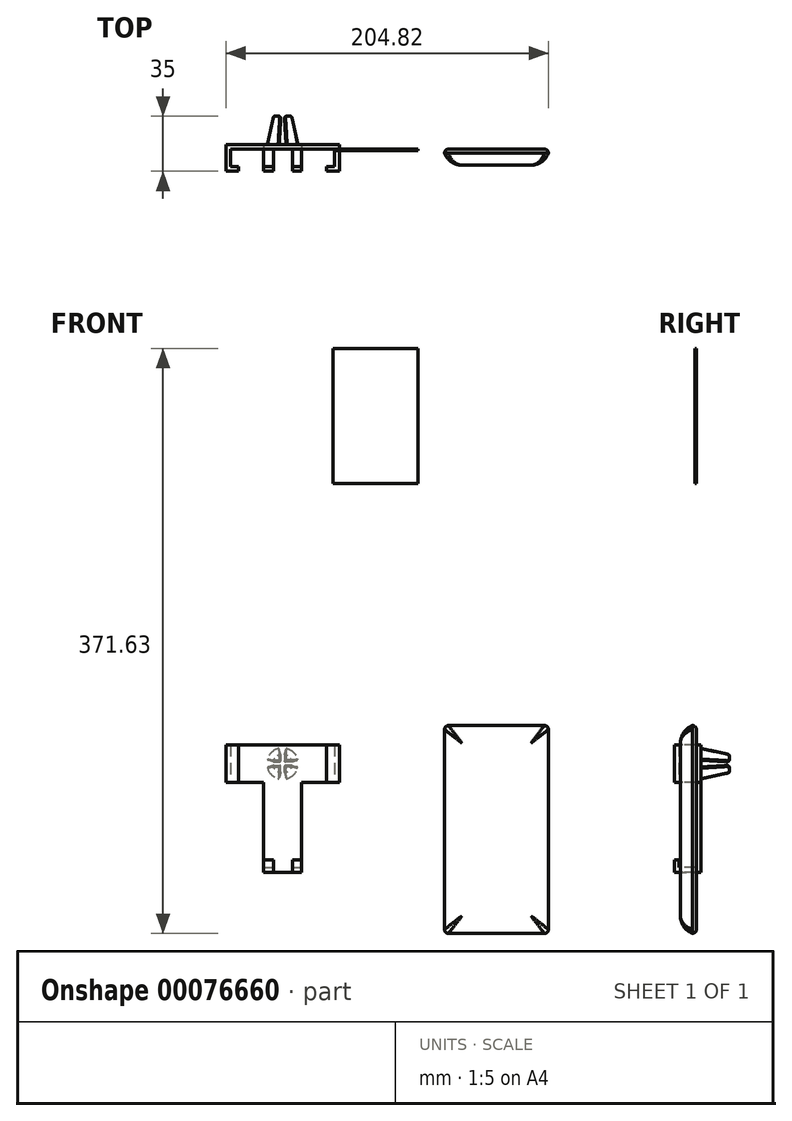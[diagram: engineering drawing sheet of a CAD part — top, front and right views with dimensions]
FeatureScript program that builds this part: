
annotation { "Feature Type Name" : "Feature", "Feature Type Description" : "" }
export const myFeature = defineFeature(function(context is Context, id is Id, definition is map)
    precondition{}
    {
        {
            var Q0;
            Q0=qCreatedBy(makeId("Front.planeOp"),FACE);
            var sketch = newSketch(context, id + "F0", { "sketchPlane" : qUnion([Q0])});
            skCircle(sketch, "E0", {"center": v(0, 0) * mm, "radius": 10 * mm});
            skSolve(sketch);
        }
        {
            var Q0;
            Q0 = qSketchRegion(id + "F0", true);
            extrude(context, id + "F1", {"entities" : qUnion([Q0]), "oppositeDirection" : true, "depth" : 3 * mm});
        }
        {
            var Q0;
            Q0=makeQuery(id+"F1.opExtrude","CAP_FACE",FACE,{"disambiguationData":[OSD([sQuery(id+"F0.wireOp",EDGE,"E0")])],"isStart":false});
            var sketch = newSketch(context, id + "F2", { "sketchPlane" : qUnion([Q0])});
            skLineSegment(sketch, "E1.top", {"start": v(-9.75, 2.2) * mm, "end": v(-2.2, 2.2) * mm});
            skLineSegment(sketch, "E1.right", {"start": v(-2.2, 9.75) * mm, "end": v(-2.2, 2.2) * mm});
            skArc(sketch, "E2", {"start": v(-2.2, 9.75) * mm, "mid": v(-7.07, 7.07) * mm, "end": v(-9.75, 2.2) * mm});
            skLineSegment(sketch, "E3.1.0", {"start": v(-9.75, -2.2) * mm, "end": v(-2.2, -2.2) * mm});
            skLineSegment(sketch, "E3.1.1", {"start": v(-2.2, -9.75) * mm, "end": v(-2.2, -2.2) * mm});
            skArc(sketch, "E3.1.2", {"start": v(-9.75, -2.2) * mm, "mid": v(-7.07, -7.07) * mm, "end": v(-2.2, -9.75) * mm});
            skLineSegment(sketch, "E3.2.0", {"start": v(2.2, -9.75) * mm, "end": v(2.2, -2.2) * mm});
            skLineSegment(sketch, "E3.2.1", {"start": v(9.75, -2.2) * mm, "end": v(2.2, -2.2) * mm});
            skArc(sketch, "E3.2.2", {"start": v(2.2, -9.75) * mm, "mid": v(7.07, -7.07) * mm, "end": v(9.75, -2.2) * mm});
            skLineSegment(sketch, "E4.2.3.0", {"start": v(9.75, 2.2) * mm, "end": v(2.2, 2.2) * mm});
            skLineSegment(sketch, "E4.3.3.0", {"start": v(2.2, 9.75) * mm, "end": v(2.2, 2.2) * mm});
            skArc(sketch, "E4.6.3.0", {"start": v(9.75, 2.2) * mm, "mid": v(7.07, 7.07) * mm, "end": v(2.2, 9.75) * mm});
            skSolve(sketch);
        }
        {
            var Q0;
            Q0=makeQuery(id+"F2.imprint","IMPRINT",FACE,{"disambiguationData":[TD([[makeQuery(id+"F2.imprint","IMPRINT",EDGE,{"derivedFrom":sQuery(id+"F2.wireOp",EDGE,"E1.top")}),-1.0]])]});
            cPlane(context, id + "F3", {"entities" : qUnion([Q0]), "cplaneType" : CPlaneType.OFFSET, "offset" : 18 * mm, "width" : 150 * mm, "height" : 150 * mm});
        }
        {
            var Q0;
            Q0=qCreatedBy(id+"F3.planeOp",FACE);
            var sketch = newSketch(context, id + "F4", { "sketchPlane" : qUnion([Q0])});
            skLineSegment(sketch, "E5.top", {"start": v(-5.9, 1.1) * mm, "end": v(-1.1, 1.1) * mm});
            skLineSegment(sketch, "E5.right", {"start": v(-1.1, 5.9) * mm, "end": v(-1.1, 1.1) * mm});
            skArc(sketch, "E6", {"start": v(-1.1, 5.9) * mm, "mid": v(-4.24, 4.24) * mm, "end": v(-5.9, 1.1) * mm});
            skLineSegment(sketch, "E7.1.0", {"start": v(-5.9, -1.1) * mm, "end": v(-1.1, -1.1) * mm});
            skLineSegment(sketch, "E7.1.1", {"start": v(-1.1, -5.9) * mm, "end": v(-1.1, -1.1) * mm});
            skArc(sketch, "E7.1.2", {"start": v(-5.9, -1.1) * mm, "mid": v(-4.24, -4.24) * mm, "end": v(-1.1, -5.9) * mm});
            skLineSegment(sketch, "E7.2.0", {"start": v(1.1, -5.9) * mm, "end": v(1.1, -1.1) * mm});
            skLineSegment(sketch, "E7.2.1", {"start": v(5.9, -1.1) * mm, "end": v(1.1, -1.1) * mm});
            skArc(sketch, "E7.2.2", {"start": v(1.1, -5.9) * mm, "mid": v(4.24, -4.24) * mm, "end": v(5.9, -1.1) * mm});
            skLineSegment(sketch, "E7.3.0", {"start": v(5.9, 1.1) * mm, "end": v(1.1, 1.1) * mm});
            skLineSegment(sketch, "E7.3.1", {"start": v(1.1, 5.9) * mm, "end": v(1.1, 1.1) * mm});
            skArc(sketch, "E7.3.2", {"start": v(5.9, 1.1) * mm, "mid": v(4.24, 4.24) * mm, "end": v(1.1, 5.9) * mm});
            skSolve(sketch);
        }
        {
            var Q1;
            Q1=makeQuery(id+"F4.imprint","IMPRINT",FACE,{"disambiguationData":[TD([[makeQuery(id+"F4.imprint","IMPRINT",EDGE,{"derivedFrom":sQuery(id+"F4.wireOp",EDGE,"E5.top")}),1.0]])]});
            var Q2;
            Q2=makeQuery(id+"F2.imprint","IMPRINT",FACE,{"disambiguationData":[TD([[makeQuery(id+"F2.imprint","IMPRINT",EDGE,{"derivedFrom":sQuery(id+"F2.wireOp",EDGE,"E1.top")}),1.0]])]});
            loft(context, id + "F5", {"operationType" : NewBodyOperationType.ADD, "sheetProfilesArray" : [{ "sheetProfileEntities" : qUnion([Q1]) }, { "sheetProfileEntities" : qUnion([Q2]) }]});
        }
        {
            var Q1;
            Q1=makeQuery(id+"F2.imprint","IMPRINT",FACE,{"disambiguationData":[TD([[makeQuery(id+"F2.imprint","IMPRINT",EDGE,{"derivedFrom":sQuery(id+"F2.wireOp",EDGE,"E4.2.3.0")}),-1.0]])]});
            var Q2;
            Q2=makeQuery(id+"F4.imprint","IMPRINT",FACE,{"disambiguationData":[TD([[makeQuery(id+"F4.imprint","IMPRINT",EDGE,{"derivedFrom":sQuery(id+"F4.wireOp",EDGE,"E7.3.0")}),-1.0]])]});
            loft(context, id + "F6", {"operationType" : NewBodyOperationType.ADD, "sheetProfilesArray" : [{ "sheetProfileEntities" : qUnion([Q1]) }, { "sheetProfileEntities" : qUnion([Q2]) }]});
        }
        {
            var Q1;
            Q1=makeQuery(id+"F2.imprint","IMPRINT",FACE,{"disambiguationData":[TD([[makeQuery(id+"F2.imprint","IMPRINT",EDGE,{"derivedFrom":sQuery(id+"F2.wireOp",EDGE,"E3.1.0")}),-1.0]])]});
            var Q2;
            Q2=makeQuery(id+"F4.imprint","IMPRINT",FACE,{"disambiguationData":[TD([[makeQuery(id+"F4.imprint","IMPRINT",EDGE,{"derivedFrom":sQuery(id+"F4.wireOp",EDGE,"E7.1.0")}),-1.0]])]});
            loft(context, id + "F7", {"operationType" : NewBodyOperationType.ADD, "sheetProfilesArray" : [{ "sheetProfileEntities" : qUnion([Q1]) }, { "sheetProfileEntities" : qUnion([Q2]) }]});
        }
        {
            var Q1;
            Q1=makeQuery(id+"F2.imprint","IMPRINT",FACE,{"disambiguationData":[TD([[makeQuery(id+"F2.imprint","IMPRINT",EDGE,{"derivedFrom":sQuery(id+"F2.wireOp",EDGE,"E3.2.0")}),-1.0]])]});
            var Q2;
            Q2=makeQuery(id+"F4.imprint","IMPRINT",FACE,{"disambiguationData":[TD([[makeQuery(id+"F4.imprint","IMPRINT",EDGE,{"derivedFrom":sQuery(id+"F4.wireOp",EDGE,"E7.2.0")}),-1.0]])]});
            loft(context, id + "F8", {"operationType" : NewBodyOperationType.ADD, "sheetProfilesArray" : [{ "sheetProfileEntities" : qUnion([Q1]) }, { "sheetProfileEntities" : qUnion([Q2]) }]});
        }
        {
            var Q0;
            {var subQ0=sQuery(id+"F4.wireOp",EDGE,"E6");var subQ1=sQuery(id+"F4.wireOp",EDGE,"E5.right");var subQ2=sQuery(id+"F4.wireOp",EDGE,"E5.top");Q0=makeQuery(id+"F5.opLoft","MID_CAP_EDGE",EDGE,{"disambiguationData":[OSD([subQ2,subQ1,subQ0]),TDD([makeQuery(id+"F4.imprint","INTERSECT",VERTEX,{"derivedFrom":[subQ2,subQ0]}),makeQuery(id+"F4.imprint","INTERSECT",VERTEX,{"derivedFrom":[subQ1,subQ0]}),makeQuery(id+"F4.imprint","IMPRINT",EDGE,{"derivedFrom":subQ0})])],"capPos":0.0});}
            var Q1;
            Q1=makeQuery(id+"F5.opLoft","SWEPT_EDGE",EDGE,{"disambiguationData":[OSD([sQuery(id+"F2.wireOp",EDGE,"E1.right"),sQuery(id+"F2.wireOp",EDGE,"E2"),sQuery(id+"F4.wireOp",EDGE,"E5.right"),sQuery(id+"F4.wireOp",EDGE,"E6")])]});
            var Q2;
            Q2=makeQuery(id+"F5.opLoft","SWEPT_EDGE",EDGE,{"disambiguationData":[OSD([sQuery(id+"F2.wireOp",EDGE,"E1.top"),sQuery(id+"F2.wireOp",EDGE,"E1.right"),sQuery(id+"F4.wireOp",EDGE,"E5.top"),sQuery(id+"F4.wireOp",EDGE,"E5.right")])]});
            var Q3;
            Q3=makeQuery(id+"F5.opLoft","SWEPT_EDGE",EDGE,{"disambiguationData":[OSD([sQuery(id+"F2.wireOp",EDGE,"E1.top"),sQuery(id+"F2.wireOp",EDGE,"E2"),sQuery(id+"F4.wireOp",EDGE,"E5.top"),sQuery(id+"F4.wireOp",EDGE,"E6")])]});
            var Q4;
            {var subQ0=sQuery(id+"F4.wireOp",EDGE,"E7.1.2");var subQ1=sQuery(id+"F4.wireOp",EDGE,"E7.1.1");var subQ2=sQuery(id+"F4.wireOp",EDGE,"E7.1.0");Q4=makeQuery(id+"F7.opLoft","MID_CAP_EDGE",EDGE,{"disambiguationData":[OSD([subQ2,subQ1,subQ0]),TDD([makeQuery(id+"F4.imprint","INTERSECT",VERTEX,{"derivedFrom":[subQ2,subQ0]}),makeQuery(id+"F4.imprint","INTERSECT",VERTEX,{"derivedFrom":[subQ1,subQ0]}),makeQuery(id+"F4.imprint","IMPRINT",EDGE,{"derivedFrom":subQ0})])],"capPos":1.0});}
            var Q5;
            Q5=makeQuery(id+"F7.opLoft","SWEPT_EDGE",EDGE,{"disambiguationData":[OSD([sQuery(id+"F2.wireOp",EDGE,"E3.1.0"),sQuery(id+"F2.wireOp",EDGE,"E3.1.2"),sQuery(id+"F4.wireOp",EDGE,"E7.1.0"),sQuery(id+"F4.wireOp",EDGE,"E7.1.2")])]});
            var Q6;
            Q6=makeQuery(id+"F7.opLoft","SWEPT_EDGE",EDGE,{"disambiguationData":[OSD([sQuery(id+"F2.wireOp",EDGE,"E3.1.0"),sQuery(id+"F2.wireOp",EDGE,"E3.1.1"),sQuery(id+"F4.wireOp",EDGE,"E7.1.0"),sQuery(id+"F4.wireOp",EDGE,"E7.1.1")])]});
            var Q7;
            Q7=makeQuery(id+"F7.opLoft","SWEPT_EDGE",EDGE,{"disambiguationData":[OSD([sQuery(id+"F2.wireOp",EDGE,"E3.1.1"),sQuery(id+"F2.wireOp",EDGE,"E3.1.2"),sQuery(id+"F4.wireOp",EDGE,"E7.1.1"),sQuery(id+"F4.wireOp",EDGE,"E7.1.2")])]});
            var Q8;
            {var subQ0=sQuery(id+"F4.wireOp",EDGE,"E7.2.2");var subQ1=sQuery(id+"F4.wireOp",EDGE,"E7.2.1");var subQ2=sQuery(id+"F4.wireOp",EDGE,"E7.2.0");Q8=makeQuery(id+"F8.opLoft","MID_CAP_EDGE",EDGE,{"disambiguationData":[OSD([subQ2,subQ1,subQ0]),TDD([makeQuery(id+"F4.imprint","INTERSECT",VERTEX,{"derivedFrom":[subQ2,subQ0]}),makeQuery(id+"F4.imprint","INTERSECT",VERTEX,{"derivedFrom":[subQ1,subQ0]}),makeQuery(id+"F4.imprint","IMPRINT",EDGE,{"derivedFrom":subQ0})])],"capPos":1.0});}
            var Q9;
            Q9=makeQuery(id+"F8.opLoft","SWEPT_EDGE",EDGE,{"disambiguationData":[OSD([sQuery(id+"F2.wireOp",EDGE,"E3.2.0"),sQuery(id+"F2.wireOp",EDGE,"E3.2.2"),sQuery(id+"F4.wireOp",EDGE,"E7.2.0"),sQuery(id+"F4.wireOp",EDGE,"E7.2.2")])]});
            var Q10;
            Q10=makeQuery(id+"F8.opLoft","SWEPT_EDGE",EDGE,{"disambiguationData":[OSD([sQuery(id+"F2.wireOp",EDGE,"E3.2.1"),sQuery(id+"F2.wireOp",EDGE,"E3.2.2"),sQuery(id+"F4.wireOp",EDGE,"E7.2.1"),sQuery(id+"F4.wireOp",EDGE,"E7.2.2")])]});
            var Q11;
            Q11=makeQuery(id+"F8.opLoft","SWEPT_EDGE",EDGE,{"disambiguationData":[OSD([sQuery(id+"F2.wireOp",EDGE,"E3.2.0"),sQuery(id+"F2.wireOp",EDGE,"E3.2.1"),sQuery(id+"F4.wireOp",EDGE,"E7.2.0"),sQuery(id+"F4.wireOp",EDGE,"E7.2.1")])]});
            var Q12;
            {var subQ0=sQuery(id+"F4.wireOp",EDGE,"E7.3.2");var subQ1=sQuery(id+"F4.wireOp",EDGE,"E7.3.1");var subQ2=sQuery(id+"F4.wireOp",EDGE,"E7.3.0");Q12=makeQuery(id+"F6.opLoft","MID_CAP_EDGE",EDGE,{"disambiguationData":[OSD([subQ2,subQ1,subQ0]),TDD([makeQuery(id+"F4.imprint","INTERSECT",VERTEX,{"derivedFrom":[subQ2,subQ0]}),makeQuery(id+"F4.imprint","INTERSECT",VERTEX,{"derivedFrom":[subQ1,subQ0]}),makeQuery(id+"F4.imprint","IMPRINT",EDGE,{"derivedFrom":subQ0})])],"capPos":1.0});}
            var Q13;
            Q13=makeQuery(id+"F6.opLoft","SWEPT_EDGE",EDGE,{"disambiguationData":[OSD([sQuery(id+"F2.wireOp",EDGE,"E4.2.3.0"),sQuery(id+"F2.wireOp",EDGE,"E4.3.3.0"),sQuery(id+"F4.wireOp",EDGE,"E7.3.0"),sQuery(id+"F4.wireOp",EDGE,"E7.3.1")])]});
            var Q14;
            Q14=makeQuery(id+"F6.opLoft","SWEPT_EDGE",EDGE,{"disambiguationData":[OSD([sQuery(id+"F2.wireOp",EDGE,"E4.2.3.0"),sQuery(id+"F2.wireOp",EDGE,"E4.6.3.0"),sQuery(id+"F4.wireOp",EDGE,"E7.3.0"),sQuery(id+"F4.wireOp",EDGE,"E7.3.2")])]});
            var Q15;
            Q15=makeQuery(id+"F6.opLoft","SWEPT_EDGE",EDGE,{"disambiguationData":[OSD([sQuery(id+"F2.wireOp",EDGE,"E4.3.3.0"),sQuery(id+"F2.wireOp",EDGE,"E4.6.3.0"),sQuery(id+"F4.wireOp",EDGE,"E7.3.1"),sQuery(id+"F4.wireOp",EDGE,"E7.3.2")])]});
            fillet(context, id + "F9", {"entities" : qUnion([Q0, Q1, Q2, Q3, Q4, Q5, Q6, Q7, Q8, Q9, Q10, Q11, Q12, Q13, Q14, Q15]), "radius" : .5 * mm, "tangentPropagation" : true, "allowEdgeOverflow" : false});
        }
        {
            var Q0;
            Q0=qCreatedBy(makeId("Front.planeOp"),FACE);
            var sketch = newSketch(context, id + "F10", { "sketchPlane" : qUnion([Q0])});
            skLineSegment(sketch, "E8.bottom", {"start": v(86.03, 177.78) * mm, "end": v(32.03, 177.78) * mm});
            skLineSegment(sketch, "E8.top", {"start": v(86.03, 263.78) * mm, "end": v(32.03, 263.78) * mm});
            skLineSegment(sketch, "E8.left", {"start": v(86.03, 177.78) * mm, "end": v(86.03, 263.78) * mm});
            skLineSegment(sketch, "E8.right", {"start": v(32.03, 177.78) * mm, "end": v(32.03, 263.78) * mm});
            skSolve(sketch);
        }
        {
            var Q0;
            Q0=makeQuery(id+"F10.imprint","IMPRINT",FACE,{"disambiguationData":[TD([[makeQuery(id+"F10.imprint","IMPRINT",EDGE,{"derivedFrom":sQuery(id+"F10.wireOp",EDGE,"E8.bottom")}),-1.0]])]});
            extrude(context, id + "F11", {"entities" : qUnion([Q0]), "depth" : 1 * mm});
        }
        {
            var Q0;
            {var subQ0=sQuery(id+"F4.wireOp",EDGE,"E5.right");var subQ1=sQuery(id+"F4.wireOp",EDGE,"E6");var subQ2=sQuery(id+"F4.wireOp",EDGE,"E5.top");Q0=makeQuery(id+"F5.opLoft","MID_CAP_EDGE",EDGE,{"disambiguationData":[OSD([subQ2,subQ0,subQ1]),TDD([makeQuery(id+"F4.imprint","INTERSECT",VERTEX,{"derivedFrom":[subQ2,subQ0]}),makeQuery(id+"F4.imprint","INTERSECT",VERTEX,{"derivedFrom":[subQ0,subQ1]}),makeQuery(id+"F4.imprint","IMPRINT",EDGE,{"derivedFrom":subQ0})])],"capPos":0.0});}
            var Q1;
            {var subQ0=sQuery(id+"F4.wireOp",EDGE,"E5.top");var subQ1=sQuery(id+"F4.wireOp",EDGE,"E5.right");var subQ2=sQuery(id+"F4.wireOp",EDGE,"E6");Q1=makeQuery(id+"F5.opLoft","MID_CAP_EDGE",EDGE,{"disambiguationData":[OSD([subQ0,subQ1,subQ2]),TDD([makeQuery(id+"F4.imprint","INTERSECT",VERTEX,{"derivedFrom":[subQ0,subQ2]}),makeQuery(id+"F4.imprint","INTERSECT",VERTEX,{"derivedFrom":[subQ0,subQ1]}),makeQuery(id+"F4.imprint","IMPRINT",EDGE,{"derivedFrom":subQ0})])],"capPos":0.0});}
            var Q2;
            {var subQ0=sQuery(id+"F4.wireOp",EDGE,"E7.1.0");var subQ1=sQuery(id+"F4.wireOp",EDGE,"E7.1.1");var subQ2=sQuery(id+"F4.wireOp",EDGE,"E7.1.2");Q2=makeQuery(id+"F7.opLoft","MID_CAP_EDGE",EDGE,{"disambiguationData":[OSD([subQ0,subQ1,subQ2]),TDD([makeQuery(id+"F4.imprint","INTERSECT",VERTEX,{"derivedFrom":[subQ0,subQ2]}),makeQuery(id+"F4.imprint","INTERSECT",VERTEX,{"derivedFrom":[subQ0,subQ1]}),makeQuery(id+"F4.imprint","IMPRINT",EDGE,{"derivedFrom":subQ0})])],"capPos":1.0});}
            var Q3;
            {var subQ0=sQuery(id+"F4.wireOp",EDGE,"E7.1.1");var subQ1=sQuery(id+"F4.wireOp",EDGE,"E7.1.2");var subQ2=sQuery(id+"F4.wireOp",EDGE,"E7.1.0");Q3=makeQuery(id+"F7.opLoft","MID_CAP_EDGE",EDGE,{"disambiguationData":[OSD([subQ2,subQ0,subQ1]),TDD([makeQuery(id+"F4.imprint","INTERSECT",VERTEX,{"derivedFrom":[subQ2,subQ0]}),makeQuery(id+"F4.imprint","INTERSECT",VERTEX,{"derivedFrom":[subQ0,subQ1]}),makeQuery(id+"F4.imprint","IMPRINT",EDGE,{"derivedFrom":subQ0})])],"capPos":1.0});}
            var Q4;
            {var subQ0=sQuery(id+"F4.wireOp",EDGE,"E7.2.0");var subQ1=sQuery(id+"F4.wireOp",EDGE,"E7.2.1");var subQ2=sQuery(id+"F4.wireOp",EDGE,"E7.2.2");Q4=makeQuery(id+"F8.opLoft","MID_CAP_EDGE",EDGE,{"disambiguationData":[OSD([subQ0,subQ1,subQ2]),TDD([makeQuery(id+"F4.imprint","INTERSECT",VERTEX,{"derivedFrom":[subQ0,subQ2]}),makeQuery(id+"F4.imprint","INTERSECT",VERTEX,{"derivedFrom":[subQ0,subQ1]}),makeQuery(id+"F4.imprint","IMPRINT",EDGE,{"derivedFrom":subQ0})])],"capPos":1.0});}
            var Q5;
            {var subQ0=sQuery(id+"F4.wireOp",EDGE,"E7.2.1");var subQ1=sQuery(id+"F4.wireOp",EDGE,"E7.2.2");var subQ2=sQuery(id+"F4.wireOp",EDGE,"E7.2.0");Q5=makeQuery(id+"F8.opLoft","MID_CAP_EDGE",EDGE,{"disambiguationData":[OSD([subQ2,subQ0,subQ1]),TDD([makeQuery(id+"F4.imprint","INTERSECT",VERTEX,{"derivedFrom":[subQ2,subQ0]}),makeQuery(id+"F4.imprint","INTERSECT",VERTEX,{"derivedFrom":[subQ0,subQ1]}),makeQuery(id+"F4.imprint","IMPRINT",EDGE,{"derivedFrom":subQ0})])],"capPos":1.0});}
            var Q6;
            {var subQ0=sQuery(id+"F4.wireOp",EDGE,"E7.3.0");var subQ1=sQuery(id+"F4.wireOp",EDGE,"E7.3.1");var subQ2=sQuery(id+"F4.wireOp",EDGE,"E7.3.2");Q6=makeQuery(id+"F6.opLoft","MID_CAP_EDGE",EDGE,{"disambiguationData":[OSD([subQ0,subQ1,subQ2]),TDD([makeQuery(id+"F4.imprint","INTERSECT",VERTEX,{"derivedFrom":[subQ0,subQ2]}),makeQuery(id+"F4.imprint","INTERSECT",VERTEX,{"derivedFrom":[subQ0,subQ1]}),makeQuery(id+"F4.imprint","IMPRINT",EDGE,{"derivedFrom":subQ0})])],"capPos":1.0});}
            var Q7;
            {var subQ0=sQuery(id+"F4.wireOp",EDGE,"E7.3.1");var subQ1=sQuery(id+"F4.wireOp",EDGE,"E7.3.2");var subQ2=sQuery(id+"F4.wireOp",EDGE,"E7.3.0");Q7=makeQuery(id+"F6.opLoft","MID_CAP_EDGE",EDGE,{"disambiguationData":[OSD([subQ2,subQ0,subQ1]),TDD([makeQuery(id+"F4.imprint","INTERSECT",VERTEX,{"derivedFrom":[subQ2,subQ0]}),makeQuery(id+"F4.imprint","INTERSECT",VERTEX,{"derivedFrom":[subQ0,subQ1]}),makeQuery(id+"F4.imprint","IMPRINT",EDGE,{"derivedFrom":subQ0})])],"capPos":1.0});}
            fillet(context, id + "F12", {"entities" : qUnion([Q0, Q1, Q2, Q3, Q4, Q5, Q6, Q7]), "radius" : 1.5 * mm, "tangentPropagation" : true, "allowEdgeOverflow" : false});
        }
        {
            var Q0;
            Q0=qCreatedBy(makeId("Front.planeOp"),FACE);
            var sketch = newSketch(context, id + "F13", { "sketchPlane" : qUnion([Q0])});
            skLineSegment(sketch, "E9.bottom", {"start": v(102.82, 24.15) * mm, "end": v(168.82, 24.15) * mm});
            skLineSegment(sketch, "E9.top", {"start": v(102.82, -107.85) * mm, "end": v(168.82, -107.85) * mm});
            skLineSegment(sketch, "E9.left", {"start": v(102.82, 24.15) * mm, "end": v(102.82, -107.85) * mm});
            skLineSegment(sketch, "E9.right", {"start": v(168.82, 24.15) * mm, "end": v(168.82, -107.85) * mm});
            skSolve(sketch);
        }
        {
            var Q0;
            Q0 = qSketchRegion(id + "F13", true);
            extrude(context, id + "F14", {"entities" : qUnion([Q0]), "depth" : 10.16 * mm});
        }
        {
            var Q0;
            Q0=makeQuery(id+"F14.opExtrude","SWEPT_EDGE",EDGE,{"disambiguationData":[OSD([sQuery(id+"F13.wireOp",EDGE,"E9.bottom"),sQuery(id+"F13.wireOp",EDGE,"E9.left")])]});
            var Q1;
            Q1=makeQuery(id+"F14.opExtrude","SWEPT_EDGE",EDGE,{"disambiguationData":[OSD([sQuery(id+"F13.wireOp",EDGE,"E9.bottom"),sQuery(id+"F13.wireOp",EDGE,"E9.right")])]});
            var Q2;
            Q2=makeQuery(id+"F14.opExtrude","SWEPT_EDGE",EDGE,{"disambiguationData":[OSD([sQuery(id+"F13.wireOp",EDGE,"E9.top"),sQuery(id+"F13.wireOp",EDGE,"E9.right")])]});
            var Q3;
            Q3=makeQuery(id+"F14.opExtrude","SWEPT_EDGE",EDGE,{"disambiguationData":[OSD([sQuery(id+"F13.wireOp",EDGE,"E9.top"),sQuery(id+"F13.wireOp",EDGE,"E9.left")])]});
            fillet(context, id + "F15", {"entities" : qUnion([Q0, Q1, Q2, Q3]), "radius" : 2.5 * mm, "tangentPropagation" : true, "allowEdgeOverflow" : false});
        }
        {
            var Q0;
            Q0=makeQuery(id+"F14.opExtrude","CAP_EDGE",EDGE,{"disambiguationData":[OSD([sQuery(id+"F13.wireOp",EDGE,"E9.right")])],"isStart":true});
            var Q1;
            Q1=makeQuery(id+"F14.opExtrude","CAP_EDGE",EDGE,{"disambiguationData":[OSD([sQuery(id+"F13.wireOp",EDGE,"E9.bottom")])],"isStart":true});
            var Q2;
            Q2=makeQuery(id+"F14.opExtrude","CAP_EDGE",EDGE,{"disambiguationData":[OSD([sQuery(id+"F13.wireOp",EDGE,"E9.left")])],"isStart":true});
            var Q3;
            Q3=makeQuery(id+"F14.opExtrude","CAP_EDGE",EDGE,{"disambiguationData":[OSD([sQuery(id+"F13.wireOp",EDGE,"E9.top")])],"isStart":true});
            fillet(context, id + "F16", {"entities" : qUnion([Q0, Q1, Q2, Q3]), "radius" : 2.5 * mm, "tangentPropagation" : true, "allowEdgeOverflow" : false});
        }
        {
            var Q0;
            Q0=makeQuery(id+"F14.opExtrude","CAP_EDGE",EDGE,{"disambiguationData":[OSD([sQuery(id+"F13.wireOp",EDGE,"E9.right")])],"isStart":false});
            var Q1;
            Q1=makeQuery(id+"F14.opExtrude","CAP_EDGE",EDGE,{"disambiguationData":[OSD([sQuery(id+"F13.wireOp",EDGE,"E9.bottom")])],"isStart":false});
            var Q2;
            Q2=makeQuery(id+"F14.opExtrude","CAP_EDGE",EDGE,{"disambiguationData":[OSD([sQuery(id+"F13.wireOp",EDGE,"E9.left")])],"isStart":false});
            var Q3;
            Q3=makeQuery(id+"F14.opExtrude","CAP_EDGE",EDGE,{"disambiguationData":[OSD([sQuery(id+"F13.wireOp",EDGE,"E9.top")])],"isStart":false});
            fillet(context, id + "F17", {"entities" : qUnion([Q0, Q1, Q2, Q3]), "radius" : 12 * mm, "tangentPropagation" : true, "allowEdgeOverflow" : false});
        }
        {
            var Q0;
            Q0=qCreatedBy(makeId("Front.planeOp"),FACE);
            var sketch = newSketch(context, id + "F18", { "sketchPlane" : qUnion([Q0])});
            skLineSegment(sketch, "E10.bottom", {"start": v(-12, -66) * mm, "end": v(12, -66) * mm});
            skLineSegment(sketch, "E10.top", {"start": v(-12, 0) * mm, "end": v(12, 0) * mm});
            skLineSegment(sketch, "E10.left", {"start": v(-12, -66) * mm, "end": v(-12, 0) * mm});
            skLineSegment(sketch, "E10.right", {"start": v(12, -66) * mm, "end": v(12, 0) * mm});
            skSolve(sketch);
        }
        {
            var Q0;
            Q0 = qSketchRegion(id + "F18", true);
            extrude(context, id + "F19", {"entities" : qUnion([Q0]), "operationType" : NewBodyOperationType.ADD, "oppositeDirection" : true, "depth" : 3 * mm});
        }
        {
            var Q0;
            Q0=makeQuery(id+"F19.opExtrude","SWEPT_FACE",FACE,{"disambiguationData":[OSD([sQuery(id+"F18.wireOp",EDGE,"E10.bottom")])]});
            var sketch = newSketch(context, id + "F20", { "sketchPlane" : qUnion([Q0])});
            skLineSegment(sketch, "E11.bottom", {"start": v(12, -3) * mm, "end": v(-12, -3) * mm});
            skLineSegment(sketch, "E11.top", {"start": v(12, 11) * mm, "end": v(-12, 11) * mm});
            skLineSegment(sketch, "E11.left", {"start": v(12, -3) * mm, "end": v(12, 11) * mm});
            skLineSegment(sketch, "E11.right", {"start": v(-12, -3) * mm, "end": v(-12, 11) * mm});
            skSolve(sketch);
        }
        {
            var Q0;
            Q0 = qSketchRegion(id + "F20", true);
            extrude(context, id + "F21", {"entities" : qUnion([Q0]), "operationType" : NewBodyOperationType.ADD, "depth" : 3 * mm});
        }
        {
            var Q0;
            Q0=qCreatedBy(makeId("Front.planeOp"),FACE);
            var sketch = newSketch(context, id + "F22", { "sketchPlane" : qUnion([Q0])});
            skLineSegment(sketch, "E12.bottom", {"start": v(33, 12) * mm, "end": v(-33, 12) * mm});
            skLineSegment(sketch, "E12.top", {"start": v(33, -12) * mm, "end": v(-33, -12) * mm});
            skLineSegment(sketch, "E12.left", {"start": v(33, 12) * mm, "end": v(33, -12) * mm});
            skLineSegment(sketch, "E12.right", {"start": v(-33, 12) * mm, "end": v(-33, -12) * mm});
            skLineSegment(sketch, "E13", {"start": v(33, 0) * mm, "end": v(-33, 0) * mm, "construction": true});
            skLineSegment(sketch, "E14", {"start": v(0, -12) * mm, "end": v(0, 12) * mm, "construction": true});
            skPoint(sketch, "E15", {"position": v(0, 0) * mm});
            skSolve(sketch);
        }
        {
            var Q0;
            Q0=makeQuery(id+"F22.imprint","IMPRINT",FACE,{"disambiguationData":[TD([[makeQuery(id+"F22.imprint","IMPRINT",EDGE,{"derivedFrom":sQuery(id+"F22.wireOp",EDGE,"E12.bottom")}),1.0]])]});
            extrude(context, id + "F23", {"entities" : qUnion([Q0]), "operationType" : NewBodyOperationType.ADD, "oppositeDirection" : true, "depth" : 3 * mm});
        }
        {
            var Q0;
            Q0=makeQuery(id+"F23.opExtrude","SWEPT_FACE",FACE,{"disambiguationData":[OSD([sQuery(id+"F22.wireOp",EDGE,"E12.right")])]});
            var sketch = newSketch(context, id + "F24", { "sketchPlane" : qUnion([Q0])});
            skLineSegment(sketch, "E16.bottom", {"start": v(-3, 12) * mm, "end": v(11, 12) * mm});
            skLineSegment(sketch, "E16.top", {"start": v(-3, -12) * mm, "end": v(11, -12) * mm});
            skLineSegment(sketch, "E16.left", {"start": v(-3, 12) * mm, "end": v(-3, -12) * mm});
            skLineSegment(sketch, "E16.right", {"start": v(11, 12) * mm, "end": v(11, -12) * mm});
            skSolve(sketch);
        }
        {
            var Q0;
            Q0 = qSketchRegion(id + "F24", true);
            extrude(context, id + "F25", {"entities" : qUnion([Q0]), "operationType" : NewBodyOperationType.ADD, "depth" : 3 * mm});
        }
        {
            var Q0;
            Q0=makeQuery(id+"F23.opExtrude","SWEPT_FACE",FACE,{"disambiguationData":[OSD([sQuery(id+"F22.wireOp",EDGE,"E12.left")])]});
            var sketch = newSketch(context, id + "F26", { "sketchPlane" : qUnion([Q0])});
            skLineSegment(sketch, "E17.bottom", {"start": v(3, -12) * mm, "end": v(-11, -12) * mm});
            skLineSegment(sketch, "E17.top", {"start": v(3, 12) * mm, "end": v(-11, 12) * mm});
            skLineSegment(sketch, "E17.left", {"start": v(3, -12) * mm, "end": v(3, 12) * mm});
            skLineSegment(sketch, "E17.right", {"start": v(-11, -12) * mm, "end": v(-11, 12) * mm});
            skSolve(sketch);
        }
        {
            var Q0;
            Q0 = qSketchRegion(id + "F26", true);
            extrude(context, id + "F27", {"entities" : qUnion([Q0]), "operationType" : NewBodyOperationType.ADD, "depth" : 3 * mm});
        }
        {
            var Q0;
            Q0=makeQuery(id+"F21.opExtrude","CAP_FACE",FACE,{"disambiguationData":[OSD([sQuery(id+"F20.wireOp",EDGE,"E11.bottom"),sQuery(id+"F20.wireOp",EDGE,"E11.top"),sQuery(id+"F20.wireOp",EDGE,"E11.left"),sQuery(id+"F20.wireOp",EDGE,"E11.right")])],"isStart":false});
            var sketch = newSketch(context, id + "F28", { "sketchPlane" : qUnion([Q0])});
            skLineSegment(sketch, "E18.bottom", {"start": v(-5.84, 11) * mm, "end": v(6.16, 11) * mm});
            skLineSegment(sketch, "E18.top", {"start": v(-5.84, 0) * mm, "end": v(6.16, 0) * mm});
            skLineSegment(sketch, "E18.left", {"start": v(-5.84, 11) * mm, "end": v(-5.84, 0) * mm});
            skLineSegment(sketch, "E18.right", {"start": v(6.16, 11) * mm, "end": v(6.16, 0) * mm});
            skSolve(sketch);
        }
        {
            var Q0;
            Q0 = qSketchRegion(id + "F28", true);
            extrude(context, id + "F29", {"entities" : qUnion([Q0]), "operationType" : NewBodyOperationType.REMOVE, "endBound" : BoundingType.UP_TO_NEXT, "oppositeDirection" : true, "depth" : 25 * mm});
        }
        {
            var Q0;
            Q0=makeQuery(id+"F25.opExtrude","SWEPT_FACE",FACE,{"disambiguationData":[OSD([sQuery(id+"F24.wireOp",EDGE,"E16.right")])]});
            var sketch = newSketch(context, id + "F30", { "sketchPlane" : qUnion([Q0])});
            skLineSegment(sketch, "E19.bottom", {"start": v(-36, -12) * mm, "end": v(-28, -12) * mm});
            skLineSegment(sketch, "E19.top", {"start": v(-36, 12) * mm, "end": v(-28, 12) * mm});
            skLineSegment(sketch, "E19.left", {"start": v(-36, -12) * mm, "end": v(-36, 12) * mm});
            skLineSegment(sketch, "E19.right", {"start": v(-28, -12) * mm, "end": v(-28, 12) * mm});
            skLineSegment(sketch, "E20.bottom", {"start": v(36, -12) * mm, "end": v(28, -12) * mm});
            skLineSegment(sketch, "E20.top", {"start": v(36, 12) * mm, "end": v(28, 12) * mm});
            skLineSegment(sketch, "E20.left", {"start": v(36, -12) * mm, "end": v(36, 12) * mm});
            skLineSegment(sketch, "E20.right", {"start": v(28, -12) * mm, "end": v(28, 12) * mm});
            skLineSegment(sketch, "E21.bottom", {"start": v(-12, -69) * mm, "end": v(-5.84, -69) * mm});
            skLineSegment(sketch, "E21.top", {"start": v(-12, -61) * mm, "end": v(-5.84, -61) * mm});
            skLineSegment(sketch, "E21.left", {"start": v(-12, -69) * mm, "end": v(-12, -61) * mm});
            skLineSegment(sketch, "E21.right", {"start": v(-5.84, -69) * mm, "end": v(-5.84, -61) * mm});
            skLineSegment(sketch, "E22.bottom", {"start": v(6.16, -69) * mm, "end": v(12, -69) * mm});
            skLineSegment(sketch, "E22.top", {"start": v(6.16, -61) * mm, "end": v(12, -61) * mm});
            skLineSegment(sketch, "E22.left", {"start": v(6.16, -69) * mm, "end": v(6.16, -61) * mm});
            skLineSegment(sketch, "E22.right", {"start": v(12, -69) * mm, "end": v(12, -61) * mm});
            skSolve(sketch);
        }
        {
            var Q0;
            Q0 = qSketchRegion(id + "F30", true);
            extrude(context, id + "F31", {"entities" : qUnion([Q0]), "operationType" : NewBodyOperationType.ADD, "depth" : 3 * mm});
        }
    });
